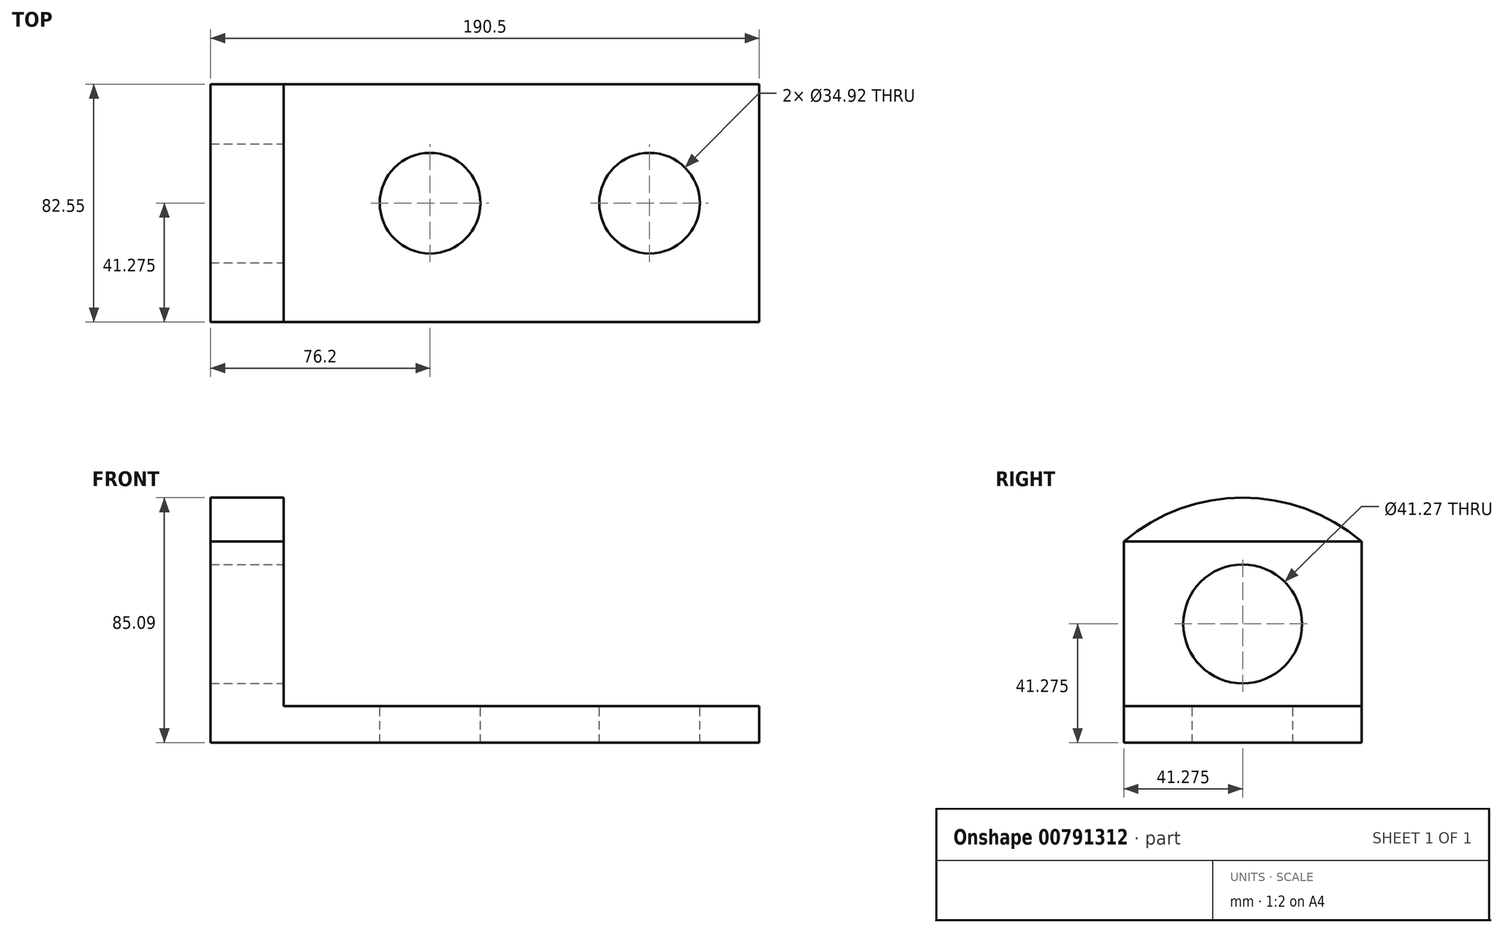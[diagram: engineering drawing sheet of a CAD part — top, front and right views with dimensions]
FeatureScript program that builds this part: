
annotation { "Feature Type Name" : "Feature", "Feature Type Description" : "" }
export const myFeature = defineFeature(function(context is Context, id is Id, definition is map)
    precondition{}
    {
        {
            var Q0;
            Q0=qCreatedBy(makeId("Front.planeOp"),FACE);
            var sketch = newSketch(context, id + "F0", { "sketchPlane" : qUnion([Q0])});
            skLineSegment(sketch, "E0", {"start": v(0, 0) * mm, "end": v(190.5, 0) * mm});
            skLineSegment(sketch, "E1", {"start": v(190.5, 0) * mm, "end": v(190.5, 12.7) * mm});
            skLineSegment(sketch, "E2", {"start": v(190.5, 12.7) * mm, "end": v(0, 12.7) * mm});
            skLineSegment(sketch, "E3", {"start": v(0, 12.7) * mm, "end": v(0, 0) * mm});
            skSolve(sketch);
        }
        {
            var Q0;
            Q0=makeQuery(id+"F0.imprint","IMPRINT",FACE,{"disambiguationData":[TD([[makeQuery(id+"F0.imprint","IMPRINT",EDGE,{"derivedFrom":sQuery(id+"F0.wireOp",EDGE,"E0")}),1.0]])]});
            extrude(context, id + "F1", {"entities" : qUnion([Q0]), "depth" : 82.55 * mm, "offsetDistance" : 25.4 * mm});
        }
        {
            var Q0;
            Q0=makeQuery(id+"F1.opExtrude","SWEPT_FACE",FACE,{"disambiguationData":[OSD([sQuery(id+"F0.wireOp",EDGE,"E2")])]});
            var sketch = newSketch(context, id + "F2", { "sketchPlane" : qUnion([Q0])});
            skLineSegment(sketch, "E4", {"start": v(0, 0) * mm, "end": v(25.4, 0) * mm});
            skLineSegment(sketch, "E5", {"start": v(25.4, 0) * mm, "end": v(25.4, -82.55) * mm});
            skLineSegment(sketch, "E6", {"start": v(25.4, -82.55) * mm, "end": v(0, -82.55) * mm});
            skLineSegment(sketch, "E7", {"start": v(0, -82.55) * mm, "end": v(0, 0) * mm});
            skSolve(sketch);
        }
        {
            var Q0;
            Q0=makeQuery(id+"F2.imprint","IMPRINT",FACE,{"disambiguationData":[TD([[makeQuery(id+"F2.imprint","IMPRINT",EDGE,{"derivedFrom":sQuery(id+"F2.wireOp",EDGE,"E4")}),1.0]])]});
            extrude(context, id + "F3", {"entities" : qUnion([Q0]), "operationType" : NewBodyOperationType.ADD, "depth" : 57.15 * mm, "offsetDistance" : 25.4 * mm});
        }
        {
            var Q0;
            Q0=makeQuery(id+"F3.opExtrude","SWEPT_FACE",FACE,{"disambiguationData":[OSD([sQuery(id+"F2.wireOp",EDGE,"E5")])]});
            var sketch = newSketch(context, id + "F4", { "sketchPlane" : qUnion([Q0])});
            skArc(sketch, "E8", {"start": v(0, 69.85) * mm, "mid": v(-41.27, 85.1) * mm, "end": v(-82.55, 69.85) * mm});
            skSolve(sketch);
        }
        {
            var Q0;
            Q0=makeQuery(id+"F4.imprint","IMPRINT",FACE,{"disambiguationData":[TD([[makeQuery(id+"F4.imprint","IMPRINT",EDGE,{"derivedFrom":sQuery(id+"F4.wireOp",EDGE,"E8")}),1.0]])]});
            extrude(context, id + "F5", {"entities" : qUnion([Q0]), "oppositeDirection" : true, "depth" : 25.4 * mm, "offsetDistance" : 25.4 * mm});
        }
        {
            var Q0;
            Q0=makeQuery(id+"F3.opExtrude","SWEPT_FACE",FACE,{"disambiguationData":[OSD([sQuery(id+"F2.wireOp",EDGE,"E5")])]});
            var sketch = newSketch(context, id + "F6", { "sketchPlane" : qUnion([Q0])});
            skLineSegment(sketch, "E9", {"start": v(-82.55, 41.28) * mm, "end": v(0, 41.28) * mm, "construction": true});
            skCircle(sketch, "E10", {"center": v(-41.28, 41.28) * mm, "radius": 20.64 * mm});
            skSolve(sketch);
        }
        {
            var Q0;
            Q0=makeQuery(id+"F6.imprint","IMPRINT",FACE,{"disambiguationData":[TD([[makeQuery(id+"F6.imprint","IMPRINT",EDGE,{"derivedFrom":sQuery(id+"F6.wireOp",EDGE,"E10")}),1.0]])]});
            extrude(context, id + "F7", {"entities" : qUnion([Q0]), "operationType" : NewBodyOperationType.REMOVE, "endBound" : BoundingType.UP_TO_NEXT, "oppositeDirection" : true, "depth" : 25.4 * mm, "offsetDistance" : 25.4 * mm});
        }
        {
            var Q0;
            Q0=makeQuery(id+"F1.opExtrude","SWEPT_FACE",FACE,{"disambiguationData":[OSD([sQuery(id+"F0.wireOp",EDGE,"E2")])]});
            var sketch = newSketch(context, id + "F8", { "sketchPlane" : qUnion([Q0])});
            skLineSegment(sketch, "E11", {"start": v(190.5, -41.28) * mm, "end": v(25.4, -41.28) * mm, "construction": true});
            skLineSegment(sketch, "E12", {"start": v(190.5, -41.28) * mm, "end": v(152.4, -41.28) * mm, "construction": true});
            skLineSegment(sketch, "E13", {"start": v(152.4, -41.28) * mm, "end": v(76.2, -41.28) * mm, "construction": true});
            skCircle(sketch, "E14", {"center": v(76.2, -41.28) * mm, "radius": 17.46 * mm});
            skCircle(sketch, "E15", {"center": v(152.4, -41.28) * mm, "radius": 17.46 * mm});
            skSolve(sketch);
        }
        {
            var Q0;
            Q0=makeQuery(id+"F8.imprint","IMPRINT",FACE,{"disambiguationData":[TD([[makeQuery(id+"F8.imprint","IMPRINT",EDGE,{"derivedFrom":sQuery(id+"F8.wireOp",EDGE,"E14")}),1.0]])]});
            var Q1;
            Q1=makeQuery(id+"F8.imprint","IMPRINT",FACE,{"disambiguationData":[TD([[makeQuery(id+"F8.imprint","IMPRINT",EDGE,{"derivedFrom":sQuery(id+"F8.wireOp",EDGE,"E15")}),1.0]])]});
            extrude(context, id + "F9", {"entities" : qUnion([Q0, Q1]), "operationType" : NewBodyOperationType.REMOVE, "endBound" : BoundingType.UP_TO_NEXT, "oppositeDirection" : true, "depth" : 25.4 * mm, "offsetDistance" : 25.4 * mm});
        }
    });
